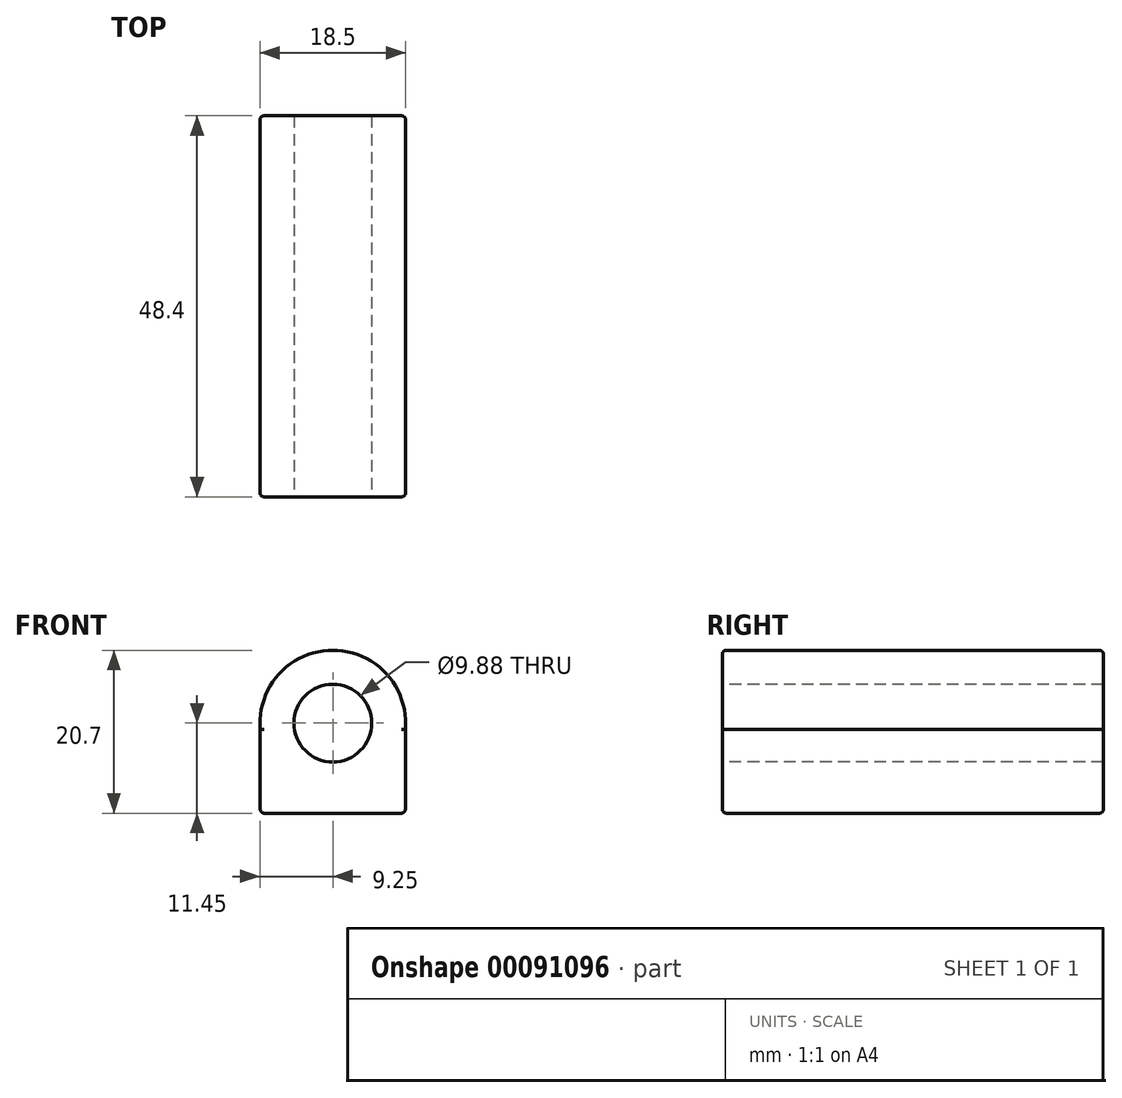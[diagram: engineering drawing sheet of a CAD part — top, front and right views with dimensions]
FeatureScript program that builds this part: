
annotation { "Feature Type Name" : "Feature", "Feature Type Description" : "" }
export const myFeature = defineFeature(function(context is Context, id is Id, definition is map)
    precondition{}
    {
        {
            var Q0;
            Q0=qCreatedBy(makeId("Front.planeOp"),FACE);
            var sketch = newSketch(context, id + "F0", { "sketchPlane" : qUnion([Q0])});
            skCircle(sketch, "E0", {"center": v(0, 0) * mm, "radius": 9.25 * mm});
            skLineSegment(sketch, "E1", {"start": v(0, 0) * mm, "end": v(0, -9.25) * mm, "construction": true});
            skLineSegment(sketch, "E2", {"start": v(0, -4.62) * mm, "end": v(-8.01, -4.62) * mm, "construction": true});
            skLineSegment(sketch, "E3.bottom", {"start": v(9.21, -9.45) * mm, "end": v(-9.21, -9.45) * mm});
            skLineSegment(sketch, "E3.top", {"start": v(9.21, 0.2) * mm, "end": v(-9.21, 0.2) * mm});
            skLineSegment(sketch, "E3.left", {"start": v(9.21, -9.45) * mm, "end": v(9.21, 0.2) * mm});
            skLineSegment(sketch, "E3.right", {"start": v(-9.21, -9.45) * mm, "end": v(-9.21, 0.2) * mm});
            skPoint(sketch, "E3.middle", {"position": v(0, -4.62) * mm});
            skSolve(sketch);
        }
        {
            var Q0;
            {var subQ5=sQuery(id+"F0.wireOp",EDGE,"E3.top");Q0=makeQuery(id+"F0.imprint","IMPRINT",FACE,{"disambiguationData":[TD([[makeQuery(id+"F0.imprint","IMPRINT",EDGE,{"derivedFrom":subQ5}),-1.0]])]});}
            var sketch = newSketch(context, id + "F1", { "sketchPlane" : qUnion([Q0])});
            skCircle(sketch, "E4", {"center": v(0, 0) * mm, "radius": 4.94 * mm});
            skSolve(sketch);
        }
        {
            var Q0;
            Q0=qSketchRegion(id+"F1",true);
            var Q1;
            {var subQ5=sQuery(id+"F0.wireOp",EDGE,"E3.top");Q1=makeQuery(id+"F0.imprint","IMPRINT",FACE,{"disambiguationData":[TD([[makeQuery(id+"F0.imprint","IMPRINT",EDGE,{"derivedFrom":subQ5}),-1.0]])]});}
            var Q2;
            {var subQ5=sQuery(id+"F0.wireOp",EDGE,"E3.top");Q2=makeQuery(id+"F0.imprint","IMPRINT",FACE,{"disambiguationData":[TD([[makeQuery(id+"F0.imprint","IMPRINT",EDGE,{"derivedFrom":subQ5}),1.0]])]});}
            var Q3;
            {var subQ5=sQuery(id+"F0.wireOp",EDGE,"E3.bottom");Q3=makeQuery(id+"F0.imprint","IMPRINT",FACE,{"disambiguationData":[TD([[makeQuery(id+"F0.imprint","IMPRINT",EDGE,{"derivedFrom":subQ5}),-1.0]])]});}
            extrude(context, id + "F2", {"entities" : qUnion([Q0, Q1, Q2, Q3]), "flatOperationType" : FlatOperationType.REMOVE, "offsetDistance" : 25 * mm, "depth" : 48.4 * mm, "domain" : OperationDomain.MODEL});
        }
        {
            var Q0;
            Q0=makeQuery(id+"F2.opExtrude","CAP_FACE",FACE,{"disambiguationData":[OSD([sQuery(id+"F1.wireOp",EDGE,"E4")])],"isStart":false});
            extrude(context, id + "F3", {"entities" : qUnion([Q0]), "operationType" : NewBodyOperationType.REMOVE, "endBound" : BoundingType.THROUGH_ALL, "oppositeDirection" : true, "depth" : 25 * mm});
        }
        {
            var Q0;
            Q0=makeQuery(id+"F2.opExtrude","SWEPT_FACE",FACE,{"disambiguationData":[OSD([sQuery(id+"F0.wireOp",EDGE,"E3.bottom")])]});
            extrude(context, id + "F4", {"entities" : qUnion([Q0]), "operationType" : NewBodyOperationType.ADD, "depth" : 2 * mm});
        }
        {
            var Q0;
            Q0=makeQuery(id+"F2.opExtrude","CAP_EDGE",EDGE,{"disambiguationData":[OSD([sQuery(id+"F0.wireOp",EDGE,"E0")])],"isStart":false});
            var Q1;
            Q1=makeQuery(id+"F2.opExtrude","CAP_EDGE",EDGE,{"disambiguationData":[OSD([sQuery(id+"F0.wireOp",EDGE,"E3.right")])],"isStart":false});
            var Q2;
            Q2=makeQuery(id+"F2.opExtrude","CAP_EDGE",EDGE,{"disambiguationData":[OSD([sQuery(id+"F0.wireOp",EDGE,"E3.left")])],"isStart":false});
            var Q3;
            Q3=makeQuery(id+"F2.opExtrude","CAP_EDGE",EDGE,{"disambiguationData":[OSD([sQuery(id+"F0.wireOp",EDGE,"E3.bottom")])],"isStart":false});
            var Q4;
            Q4=makeQuery(id+"F2.opExtrude","CAP_EDGE",EDGE,{"disambiguationData":[OSD([sQuery(id+"F0.wireOp",EDGE,"E3.bottom")])],"isStart":true});
            var Q5;
            Q5=makeQuery(id+"F2.opExtrude","CAP_EDGE",EDGE,{"disambiguationData":[OSD([sQuery(id+"F0.wireOp",EDGE,"E3.left")])],"isStart":true});
            var Q6;
            Q6=makeQuery(id+"F2.opExtrude","CAP_EDGE",EDGE,{"disambiguationData":[OSD([sQuery(id+"F0.wireOp",EDGE,"E3.right")])],"isStart":true});
            var Q7;
            Q7=makeQuery(id+"F2.opExtrude","CAP_EDGE",EDGE,{"disambiguationData":[OSD([sQuery(id+"F0.wireOp",EDGE,"E0")])],"isStart":true});
            var Q8;
            Q8=makeQuery(id+"F2.opExtrude","SWEPT_EDGE",EDGE,{"disambiguationData":[OSD([sQuery(id+"F0.wireOp",EDGE,"E3.bottom"),sQuery(id+"F0.wireOp",EDGE,"E3.right")])]});
            var Q9;
            Q9=makeQuery(id+"F2.opExtrude","SWEPT_EDGE",EDGE,{"disambiguationData":[OSD([sQuery(id+"F0.wireOp",EDGE,"E3.bottom"),sQuery(id+"F0.wireOp",EDGE,"E3.left")])]});
            fillet(context, id + "F5", {"entities" : qUnion([Q0, Q1, Q2, Q3, Q4, Q5, Q6, Q7, Q8, Q9]), "radius" : .5 * mm, "tangentPropagation" : true, "allowEdgeOverflow" : false});
        }
        {
            var Q0;
            Q0=makeQuery(id+"F4.opExtrude","CAP_EDGE",EDGE,{"disambiguationData":[OSD([sQuery(id+"F0.wireOp",EDGE,"E3.bottom"),sQuery(id+"F0.wireOp",EDGE,"E3.left")])],"isStart":false});
            var Q1;
            {var subQ0=sQuery(id+"F0.wireOp",EDGE,"E3.bottom");Q1=makeQuery(id+"F4.opExtrude","CAP_EDGE",EDGE,{"disambiguationData":[OSD([subQ0]),TDD([makeQuery(id+"F2.opExtrude","CAP_EDGE",EDGE,{"disambiguationData":[OSD([subQ0])],"isStart":true})])],"isStart":false});}
            var Q2;
            {var subQ0=sQuery(id+"F0.wireOp",EDGE,"E3.bottom");Q2=makeQuery(id+"F4.opExtrude","CAP_EDGE",EDGE,{"disambiguationData":[OSD([subQ0]),TDD([makeQuery(id+"F2.opExtrude","CAP_EDGE",EDGE,{"disambiguationData":[OSD([subQ0])],"isStart":false})])],"isStart":false});}
            var Q3;
            Q3=makeQuery(id+"F4.opExtrude","CAP_EDGE",EDGE,{"disambiguationData":[OSD([sQuery(id+"F0.wireOp",EDGE,"E3.bottom"),sQuery(id+"F0.wireOp",EDGE,"E3.right")])],"isStart":false});
            fillet(context, id + "F6", {"entities" : qUnion([Q0, Q1, Q2, Q3]), "radius" : .5 * mm, "tangentPropagation" : true, "allowEdgeOverflow" : false});
        }
    });
